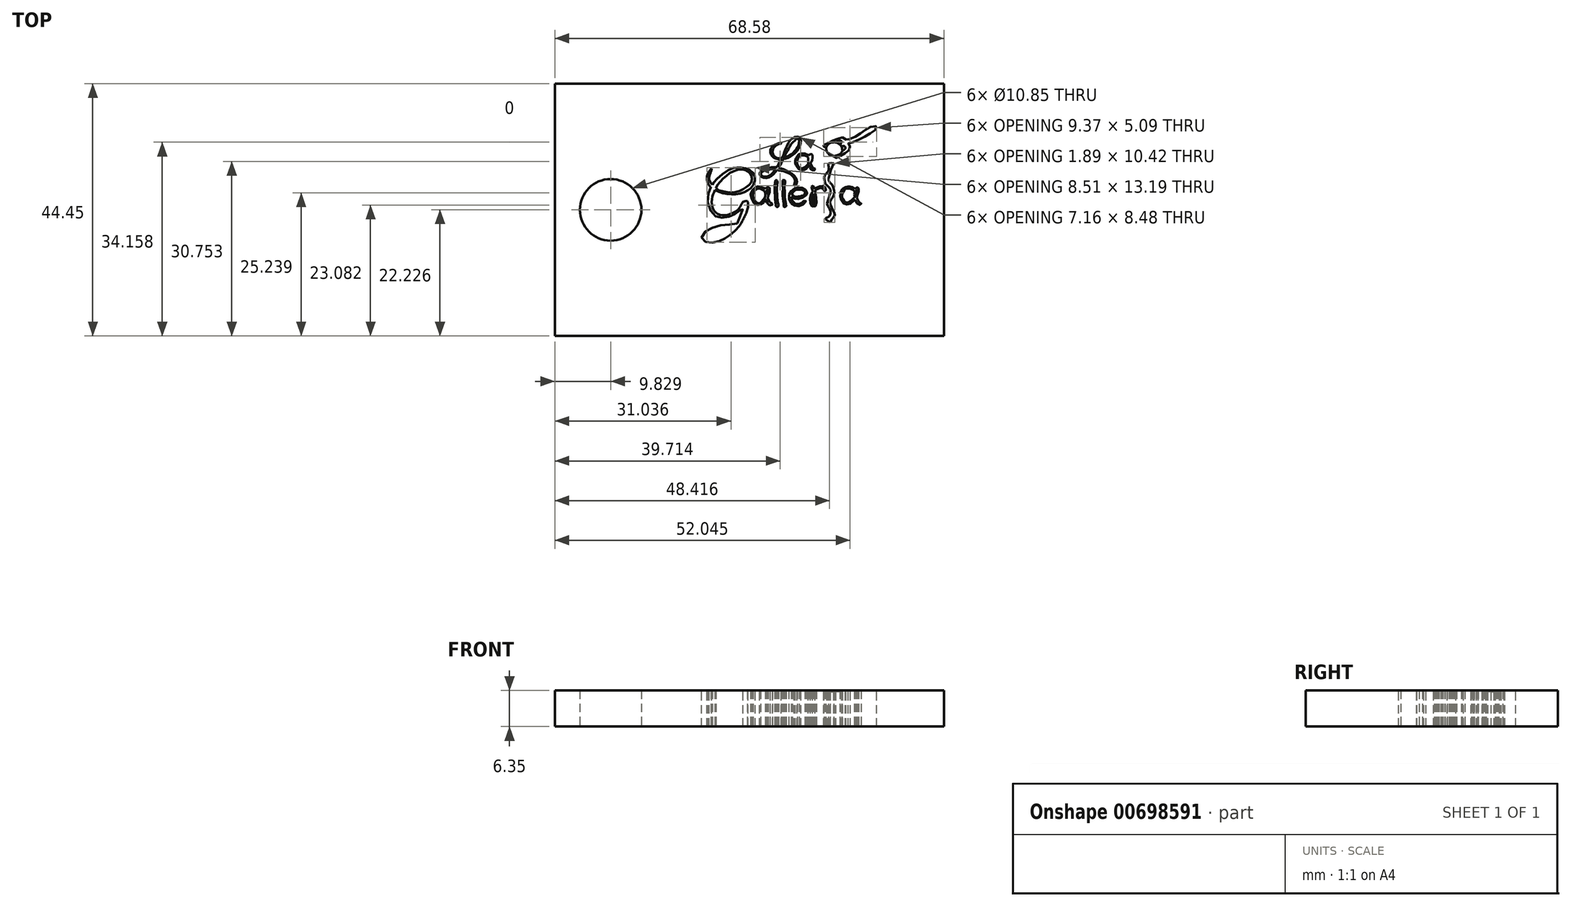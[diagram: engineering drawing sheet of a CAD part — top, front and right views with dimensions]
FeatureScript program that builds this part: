
annotation { "Feature Type Name" : "Feature", "Feature Type Description" : "" }
export const myFeature = defineFeature(function(context is Context, id is Id, definition is map)
    precondition{}
    {
        {
            var Q0;
            Q0=qCreatedBy(makeId("Top.planeOp"),FACE);
            var sketch = newSketch(context, id + "F0", { "sketchPlane" : qUnion([Q0])});
            skLineSegment(sketch, "E0.bottom", {"start": v(-33.84, -40.5) * mm, "end": v(34.74, -40.5) * mm});
            skLineSegment(sketch, "E0.top", {"start": v(-33.84, -84.96) * mm, "end": v(34.74, -84.96) * mm});
            skLineSegment(sketch, "E0.left", {"start": v(-33.84, -40.5) * mm, "end": v(-33.84, -84.96) * mm});
            skLineSegment(sketch, "E0.right", {"start": v(34.74, -40.5) * mm, "end": v(34.74, -84.96) * mm});
            skCircle(sketch, "E1", {"center": v(-24.01, -62.73) * mm, "radius": 5.42 * mm});
            skLineSegment(sketch, "E2", {"start": v(34.74, -62.73) * mm, "end": v(-33.84, -62.73) * mm, "construction": true});
            skSolve(sketch);
        }
        {
            var Q0;
            Q0=makeQuery(id+"F0.imprint","IMPRINT",FACE,{"disambiguationData":[TD([[makeQuery(id+"F0.imprint","IMPRINT",EDGE,{"derivedFrom":sQuery(id+"F0.wireOp",EDGE,"E0.bottom")}),-1.0]])]});
            extrude(context, id + "F1", {"entities" : qUnion([Q0]), "depth" : 6.35 * mm, "offsetDistance" : 25.4 * mm});
        }
        {
            var Q0;
            Q0=qCreatedBy(makeId("Top.planeOp"),FACE);
            var sketch = newSketch(context, id + "F2", { "sketchPlane" : qUnion([Q0])});
            skFitSpline(sketch, "E3", {"points": [v(8.83, -74.2) * mm, v(6.32, -74.67) * mm, v(3.86, -74.8) * mm, v(2.14, -74.58) * mm, v(0.76, -74.1) * mm, v(-0.5, -72.85) * mm, v(-0.7, -72.2) * mm, v(-0.7, -71.6) * mm, v(-0.36, -71.21) * mm, v(0.02, -71) * mm, v(-0.54, -70.7) * mm, v(-1.05, -69.92) * mm, v(-1.31, -68.93) * mm, v(-1.01, -67.85) * mm, v(-0.54, -67.2) * mm, v(-0.1, -66.98) * mm, v(-0.23, -66.55) * mm, v(-0.23, -66.04) * mm, v(0.02, -65.65) * mm, v(0.28, -65.26) * mm, v(0.71, -64.91) * mm, v(1.45, -64.36) * mm, v(2.06, -64.36) * mm, v(2.61, -64.36) * mm, v(3.78, -63.96) * mm, v(4.81, -64.36) * mm, v(4.81, -64.36) * mm, v(5.9, -65.13) * mm, v(6.32, -66.04) * mm, v(6.84, -66.42) * mm, v(7.62, -66.77) * mm, v(8.05, -67.2) * mm], "startDerivative": vector(-44.88, -9.77) * mm, "endDerivative": vector(13.58, -17.29) * mm});
            skFitSpline(sketch, "E4", {"points": [v(7.93, -67.04) * mm, v(7.02, -67.04) * mm, v(6.32, -66.42) * mm, v(5.46, -65.6) * mm, v(4.94, -65.09) * mm, v(3.78, -64.36) * mm, v(2.61, -64.36) * mm, v(1.8, -64.91) * mm, v(0.71, -65.34) * mm, v(0.33, -66.42) * mm, v(0.71, -67.59) * mm, v(1.5, -68.06) * mm, v(2, -68.28) * mm, v(1.62, -68.67) * mm, v(0.71, -68.1) * mm, v(0.24, -67.46) * mm, v(-0.1, -66.98) * mm], "startDerivative": vector(-15.93, -2.47) * mm, "endDerivative": vector(-7.03, 9.38) * mm});
            skFitSpline(sketch, "E5", {"points": [v(15.3, -54.51) * mm, v(14.74, -55.9) * mm, v(14.52, -56.76) * mm, v(14.44, -57.58) * mm, v(15, -58.27) * mm, v(15.39, -59.26) * mm, v(15.43, -59.86) * mm, v(15.09, -60.6) * mm, v(14.65, -61.33) * mm, v(14.87, -62.15) * mm, v(15.26, -62.97) * mm, v(15.52, -63.66) * mm, v(15, -64.36) * mm, v(14.3, -65.26) * mm, v(13.83, -64.36) * mm, v(14.4, -63.96) * mm, v(14.7, -63.53) * mm, v(14.74, -63.06) * mm, v(14.52, -62.45) * mm, v(14.14, -61.72) * mm, v(14.4, -60.86) * mm], "startDerivative": vector(-9.76, -21.95) * mm, "endDerivative": vector(8.6, 17.1) * mm});
            skFitSpline(sketch, "E6", {"points": [v(14.4, -60.86) * mm, v(14.65, -59.86) * mm, v(14.65, -59) * mm, v(13.96, -58.27) * mm, v(13.66, -57.5) * mm, v(13.75, -56.63) * mm, v(14.4, -55.8) * mm, v(14.4, -54.99) * mm, v(14.4, -54.6) * mm, v(15.3, -54.51) * mm], "startDerivative": vector(2.25, 8.11) * mm, "endDerivative": vector(10.26, -0.46) * mm});
            skFitSpline(sketch, "E7", {"points": [v(14.67, -64.93) * mm, v(16.12, -64.36) * mm, v(17.07, -63.96) * mm, v(17.8, -63.92) * mm, v(18.8, -64.36) * mm, v(19.36, -65.26) * mm, v(19.53, -66.47) * mm, v(19.62, -66.81) * mm, v(19.14, -67.5) * mm, v(19.49, -67.46) * mm, v(19.83, -67.68) * mm, v(19.83, -68.06) * mm, v(20.3, -68.02) * mm, v(20.87, -68.02) * mm, v(20.87, -68.58) * mm, v(20.82, -68.8) * mm, v(21.26, -68.62) * mm, v(21.69, -68.8) * mm, v(21.56, -69.32) * mm, v(20.74, -69.88) * mm, v(21.13, -70.3) * mm, v(21.64, -70.83) * mm, v(21.77, -71.6) * mm, v(21.13, -72.5) * mm, v(19.7, -73.46) * mm, v(18.15, -74.28) * mm, v(16.42, -74.58) * mm, v(14.61, -74.7) * mm, v(12.67, -74.54) * mm, v(11.29, -73.89) * mm, v(10.04, -73.93) * mm, v(8.83, -74.2) * mm], "startDerivative": vector(35.2, 13.5) * mm, "endDerivative": vector(-31.28, -7.01) * mm});
            skFitSpline(sketch, "E8", {"points": [v(13.83, -64.36) * mm, v(12.71, -63.96) * mm, v(10.73, -63.49) * mm, v(8, -63.96) * mm, v(6.8, -65.13) * mm, v(6.32, -66.04) * mm], "startDerivative": vector(-6.29, 2.24) * mm, "endDerivative": vector(-2.62, -5.65) * mm});
            skFitSpline(sketch, "E9", {"points": [v(0.24, -67.46) * mm, v(0.24, -68.5) * mm, v(-0.2, -69.23) * mm, v(0.24, -70.3) * mm, v(1.23, -71) * mm, v(3.86, -71.34) * mm, v(6.32, -71) * mm, v(8.1, -69.83) * mm, v(8.87, -68.58) * mm, v(9.09, -68.1) * mm, v(9.6, -68.1) * mm, v(9.43, -69.1) * mm, v(8.7, -70.05) * mm, v(7.06, -71.43) * mm, v(5.6, -72) * mm, v(3.95, -71.95) * mm, v(2.48, -71.82) * mm, v(0.71, -71.47) * mm, v(0.02, -71) * mm], "startDerivative": vector(3.87, -23.1) * mm, "endDerivative": vector(-13.05, 11.9) * mm});
            skFitSpline(sketch, "E10", {"points": [v(6.46, -65.74) * mm, v(6.84, -65.74) * mm, v(7.16, -65.13) * mm, v(8.05, -64.56) * mm, v(8.95, -64.15) * mm, v(9.81, -64) * mm, v(10.76, -63.93) * mm, v(11.8, -64.04) * mm, v(12.81, -64.36) * mm, v(13.48, -64.94) * mm, v(13.4, -65.74) * mm, v(12.9, -66.04) * mm, v(13.03, -65.5) * mm, v(12.81, -65.13) * mm, v(12.23, -64.9) * mm, v(11.02, -65.13) * mm, v(10.57, -65.33) * mm], "startDerivative": vector(9.8, -2.5) * mm, "endDerivative": vector(-7.4, -3.9) * mm});
            skFitSpline(sketch, "E11", {"points": [v(19.53, -66.47) * mm, v(19.07, -66.24) * mm, v(18.47, -66.47) * mm, v(18.36, -66.47) * mm], "startDerivative": vector(-1.06, 0.92) * mm, "endDerivative": vector(-0.47, 0.13) * mm});
            skFitSpline(sketch, "E12", {"points": [v(18.47, -66.47) * mm, v(18.7, -65.79) * mm, v(18.66, -65.29) * mm, v(18.47, -64.99) * mm, v(17.71, -64.77) * mm, v(16.7, -64.82) * mm, v(15.66, -65.25) * mm, v(14.82, -65.57) * mm, v(14.15, -65.87) * mm, v(13.53, -66.22) * mm, v(12.5, -66.8) * mm, v(11.86, -67.08) * mm, v(11.28, -67.32) * mm, v(10.63, -67.21) * mm, v(11.28, -66.8) * mm, v(11.41, -66.47) * mm, v(11.67, -66.47) * mm, v(12.34, -66.47) * mm, v(12.9, -66.04) * mm], "startDerivative": vector(5.46, 12.2) * mm, "endDerivative": vector(9.08, 9.58) * mm});
            skFitSpline(sketch, "E13", {"points": [v(0.21, -71.17) * mm, v(0.52, -71.38) * mm, v(0.21, -71.48) * mm, v(-0.07, -71.83) * mm, v(0, -72.52) * mm, v(0.21, -73.06) * mm, v(0.84, -73.4) * mm, v(1.74, -73.77) * mm, v(2.76, -73.99) * mm, v(3.86, -73.96) * mm, v(4.92, -74.03) * mm, v(5.7, -74) * mm, v(6.32, -74.03) * mm, v(7.25, -74.03) * mm, v(7.46, -73.88) * mm, v(6.51, -73.7) * mm, v(5.97, -73.6) * mm, v(5.2, -73.34) * mm, v(5, -73.17) * mm, v(4.85, -73.3) * mm, v(4.23, -73.34) * mm, v(3.64, -73.27) * mm, v(3.17, -73.25) * mm, v(2.35, -73.1) * mm, v(1.68, -72.84) * mm, v(1.16, -72.52) * mm, v(0.92, -72.02) * mm, v(0.91, -71.54) * mm, v(0.71, -71.47) * mm], "startDerivative": vector(17.38, -8.75) * mm, "endDerivative": vector(-11.59, 0.94) * mm});
            skFitSpline(sketch, "E14", {"points": [v(2.05, -71.77) * mm, v(1.87, -71.95) * mm, v(1.85, -72.24) * mm, v(2.09, -72.41) * mm, v(2.74, -72.52) * mm, v(3.34, -72.6) * mm, v(3.77, -72.67) * mm, v(3.95, -72.7) * mm, v(3.66, -72.45) * mm, v(3.38, -72.15) * mm, v(3.22, -71.89) * mm], "startDerivative": vector(-2.45, -1.9) * mm, "endDerivative": vector(-1.73, 2.9) * mm});
            skFitSpline(sketch, "E15", {"points": [v(3.95, -72.7) * mm, v(4.36, -72.89) * mm, v(4.77, -73.12) * mm, v(5, -73.17) * mm], "startDerivative": vector(1.1, -0.47) * mm, "endDerivative": vector(0.85, -0.05) * mm});
            skFitSpline(sketch, "E16", {"points": [v(7.46, -73.88) * mm, v(8.2, -73.88) * mm, v(9.3, -73.7) * mm, v(10.44, -73.42) * mm, v(11.02, -73.17) * mm, v(11.67, -72.7) * mm, v(12.08, -72.22) * mm, v(12.14, -71.63) * mm, v(12.3, -71.16) * mm, v(12.3, -71.03) * mm, v(11.78, -70.92) * mm, v(10.83, -70.77) * mm, v(10.33, -70.68) * mm, v(9.43, -70.43) * mm, v(8.84, -70.23) * mm, v(8.5, -70.24) * mm, v(7.7, -70.95) * mm], "startDerivative": vector(10.73, -0.44) * mm, "endDerivative": vector(-11.05, -11.71) * mm});
            skFitSpline(sketch, "E17", {"points": [v(4.61, -72) * mm, v(5, -72.32) * mm, v(5.54, -72.7) * mm, v(6.32, -73) * mm, v(6.51, -73.17) * mm, v(7.46, -73.42) * mm, v(8.48, -73.4) * mm, v(9.53, -73.17) * mm, v(10.44, -72.97) * mm, v(11.2, -72.24) * mm, v(11.67, -71.74) * mm, v(11.78, -70.92) * mm, v(11.43, -70.87) * mm, v(11.03, -70.8) * mm, v(10.94, -71.35) * mm, v(10.6, -71.98) * mm, v(9.88, -72.37) * mm, v(8.65, -72.7) * mm, v(8, -72.7) * mm, v(6.82, -72.48) * mm, v(6.32, -72.26) * mm, v(5.9, -71.94) * mm, v(6.32, -71.81) * mm, v(6.84, -71.56) * mm, v(7.23, -71.98) * mm, v(8, -72.13) * mm, v(9.04, -71.94) * mm, v(9.73, -71.57) * mm, v(10.16, -71.2) * mm, v(10.33, -70.68) * mm, v(9.98, -70.6) * mm, v(9.59, -70.48) * mm, v(9.43, -70.92) * mm, v(8.95, -71.3) * mm, v(8, -71.57) * mm, v(7.27, -71.28) * mm, v(7.7, -70.95) * mm, v(8, -70.95) * mm, v(8.4, -70.95) * mm, v(8.89, -70.68) * mm, v(9.12, -70.32) * mm], "startDerivative": vector(17.49, -14.44) * mm, "endDerivative": vector(9.15, 18.57) * mm});
            skFitSpline(sketch, "E18", {"points": [v(9, -69.73) * mm, v(9.3, -69.98) * mm, v(9.98, -70.13) * mm, v(10.48, -70.13) * mm, v(11.67, -70.43) * mm, v(12.3, -70.6) * mm, v(13.56, -70.68) * mm, v(14.52, -70.68) * mm, v(15.46, -70.32) * mm, v(16.96, -69.94) * mm, v(17.9, -69.46) * mm, v(19, -68.96) * mm, v(20.3, -68.02) * mm], "startDerivative": vector(4.52, -5.15) * mm, "endDerivative": vector(12.09, 9.8) * mm});
            skFitSpline(sketch, "E19", {"points": [v(20.82, -68.8) * mm, v(20.5, -68.96) * mm, v(19.87, -69.33) * mm, v(19.1, -69.67) * mm, v(18.64, -69.89) * mm, v(17.83, -70.25) * mm, v(17.22, -70.48) * mm, v(16.32, -70.67) * mm, v(15.46, -70.95) * mm, v(14.02, -71.16) * mm, v(12.78, -71.05) * mm, v(12.3, -71.03) * mm, v(12.2, -71.4) * mm, v(12.13, -71.77) * mm, v(12.5, -71.78) * mm, v(13, -71.63) * mm, v(13.36, -71.43) * mm, v(13.4, -71.16) * mm], "startDerivative": vector(-6.76, -3.18) * mm, "endDerivative": vector(-0.09, 7.44) * mm});
            skFitSpline(sketch, "E20", {"points": [v(9.37, -69.21) * mm, v(9.88, -69.39) * mm, v(10.44, -69.53) * mm, v(10.97, -69.73) * mm, v(11.93, -70.08) * mm, v(12.77, -70.25) * mm, v(13.27, -70.33) * mm, v(14.47, -70.14) * mm, v(15.09, -69.82) * mm, v(15.94, -69.46) * mm, v(16.88, -68.96) * mm, v(18.01, -68.56) * mm, v(18.7, -68.23) * mm, v(19.3, -67.5) * mm, v(19.2, -67.4) * mm, v(17.94, -67.73) * mm, v(17.24, -68.08) * mm, v(16.56, -68.36) * mm, v(16.46, -68.42) * mm, v(16.28, -68.67) * mm, v(16.04, -68.96) * mm, v(15.55, -69.14) * mm, v(15.13, -69.22) * mm, v(14.73, -69.49) * mm, v(14.13, -69.73) * mm, v(13.7, -69.82) * mm, v(13.24, -69.82) * mm, v(12.83, -69.6) * mm, v(12.14, -69.35) * mm, v(11.19, -68.96) * mm, v(10.26, -68.8) * mm, v(9.9, -68.8) * mm, v(9.56, -68.8) * mm], "startDerivative": vector(17.22, -6.4) * mm, "endDerivative": vector(-15.28, 0.15) * mm});
            skFitSpline(sketch, "E21", {"points": [v(0.37, -66.83) * mm, v(0.79, -66.8) * mm, v(1.2, -66.77) * mm, v(1.68, -66.66) * mm, v(2.42, -66.46) * mm, v(3.32, -66.21) * mm, v(4.18, -66.17) * mm, v(5, -66.1) * mm, v(5.6, -66) * mm, v(5.92, -66.03) * mm], "startDerivative": vector(4.5, 0.34) * mm, "endDerivative": vector(3.66, -0.47) * mm});
            skFitSpline(sketch, "E22", {"points": [v(1.2, -66.77) * mm, v(1.2, -66.42) * mm, v(1.38, -65.88) * mm, v(1.74, -65.5) * mm, v(2.32, -65.4) * mm, v(3, -65.57) * mm, v(3.85, -65.82) * mm, v(4.5, -65.9) * mm, v(5.13, -66.08) * mm], "startDerivative": vector(-0.3, 3.46) * mm, "endDerivative": vector(4.87, -1.51) * mm});
            skFitSpline(sketch, "E23", {"points": [v(0.51, -67.25) * mm, v(1.2, -67.2) * mm, v(1.94, -67.1) * mm, v(3.35, -66.77) * mm, v(4.52, -66.42) * mm, v(6.32, -66.42) * mm], "startDerivative": vector(4.45, 0.36) * mm, "endDerivative": vector(7.71, -0.5) * mm});
            skFitSpline(sketch, "E24", {"points": [v(0.71, -67.59) * mm, v(1.73, -67.59) * mm, v(2.93, -67.43) * mm, v(4.18, -67.2) * mm, v(4.85, -67.04) * mm, v(6.47, -66.82) * mm, v(6.7, -66.82) * mm], "startDerivative": vector(5.79, -0.2) * mm, "endDerivative": vector(1.9, -0.15) * mm});
            skFitSpline(sketch, "E25", {"points": [v(2, -68.28) * mm, v(2.6, -68.06) * mm, v(3.6, -67.9) * mm, v(3.84, -67.74) * mm, v(4.26, -67.59) * mm, v(4.76, -67.45) * mm, v(5, -67.45) * mm, v(5.23, -67.37) * mm, v(5.63, -67.24) * mm, v(6.5, -67.1) * mm, v(7.6, -67.1) * mm], "startDerivative": vector(4.6, 2.3) * mm, "endDerivative": vector(7.8, -0.3) * mm});
            skFitSpline(sketch, "E26", {"points": [v(3.6, -67.9) * mm, v(3.39, -68.26) * mm, v(3.3, -68.51) * mm, v(3.45, -69.06) * mm, v(3.92, -69.4) * mm, v(4.5, -69.57) * mm, v(5.05, -69.62) * mm, v(5.79, -69.42) * mm, v(6.32, -68.94) * mm, v(6.45, -68.4) * mm, v(6.12, -67.9) * mm, v(5.56, -67.59) * mm, v(4.87, -67.45) * mm], "startDerivative": vector(-3.32, -5.44) * mm, "endDerivative": vector(-7.66, 1.04) * mm});
            skFitSpline(sketch, "E27", {"points": [v(0.71, -68.1) * mm, v(0.71, -68.57) * mm, v(0.58, -69.13) * mm, v(0.6, -69.64) * mm, v(0.84, -70.07) * mm, v(1.4, -70.43) * mm, v(2.22, -70.67) * mm, v(2.88, -70.7) * mm, v(3.6, -70.75) * mm, v(4.13, -70.72) * mm, v(5, -70.6) * mm, v(5.79, -70.4) * mm, v(6.72, -70) * mm, v(7.54, -69.48) * mm, v(8.25, -68.79) * mm, v(8.48, -68.1) * mm, v(8.5, -67.73) * mm], "startDerivative": vector(0.7, -8.8) * mm, "endDerivative": vector(0.25, 7.53) * mm});
            skFitSpline(sketch, "E28", {"points": [v(1.5, -68.67) * mm, v(1.8, -68.79) * mm, v(2.46, -68.67) * mm, v(3.3, -68.51) * mm], "startDerivative": vector(1.1, -0.65) * mm, "endDerivative": vector(2.11, 0.34) * mm});
            skFitSpline(sketch, "E29", {"points": [v(6.12, -67.9) * mm, v(6.48, -67.77) * mm, v(7.2, -67.73) * mm, v(8, -67.73) * mm, v(8.5, -67.73) * mm, v(9.16, -67.9) * mm, v(10.07, -68.28) * mm, v(10.94, -68.67) * mm, v(12.39, -69.1) * mm, v(13.4, -69.25) * mm, v(14.73, -69.26) * mm, v(15.13, -69.22) * mm], "startDerivative": vector(5.23, 2.4) * mm, "endDerivative": vector(5.1, 0.8) * mm});
            skFitSpline(sketch, "E30", {"points": [v(8.05, -67.2) * mm, v(8.84, -67.37) * mm, v(10.03, -67.73) * mm, v(10.84, -68.1) * mm, v(11.9, -68.51) * mm, v(13.53, -68.93) * mm, v(14, -69.05) * mm], "startDerivative": vector(4.93, -0.95) * mm, "endDerivative": vector(3.36, -0.83) * mm});
            skFitSpline(sketch, "E31", {"points": [v(6.6, -65.78) * mm, v(7.34, -65.9) * mm, v(7.95, -66.08) * mm, v(8.44, -66.21) * mm], "startDerivative": vector(2.05, -0.29) * mm, "endDerivative": vector(1.57, -0.4) * mm});
            skFitSpline(sketch, "E32", {"points": [v(6.6, -66.3) * mm, v(7.04, -66.24) * mm, v(7.59, -66.37) * mm, v(8.3, -66.58) * mm, v(8.69, -66.8) * mm], "startDerivative": vector(1.9, 0.45) * mm, "endDerivative": vector(1.55, -0.98) * mm});
            skFitSpline(sketch, "E33", {"points": [v(7.34, -65.9) * mm, v(7.59, -65.48) * mm, v(8.3, -65.03) * mm, v(9.72, -64.6) * mm, v(11.07, -64.36) * mm, v(12.7, -64.58) * mm, v(13.15, -64.94) * mm, v(13.4, -65.74) * mm], "startDerivative": vector(2, 4.32) * mm, "endDerivative": vector(1.5, -6.77) * mm});
            skFitSpline(sketch, "E34", {"points": [v(11.32, -65.74) * mm, v(11.57, -65.74) * mm, v(11.94, -65.74) * mm, v(12.3, -66.04) * mm, v(12.34, -66.47) * mm], "startDerivative": vector(1.18, -0.06) * mm, "endDerivative": vector(-0.17, -1.68) * mm});
            skFitSpline(sketch, "E35", {"points": [v(8.44, -66.21) * mm, v(8.44, -66.02) * mm, v(8.67, -65.65) * mm, v(9.05, -65.39) * mm, v(9.64, -65.21) * mm, v(10.25, -65.22) * mm, v(10.7, -65.35) * mm, v(11.15, -65.59) * mm, v(11.38, -65.97) * mm, v(11.41, -66.47) * mm, v(11.14, -66.91) * mm, v(10.46, -67.21) * mm, v(9.72, -67.26) * mm, v(9.1, -67.1) * mm, v(8.69, -66.8) * mm, v(8.44, -66.52) * mm, v(8.36, -66.17) * mm, v(8.69, -65.6) * mm], "startDerivative": vector(-0.8, 4.83) * mm, "endDerivative": vector(6.62, 8.74) * mm});
            skFitSpline(sketch, "E36", {"points": [v(7.62, -66.77) * mm, v(7.91, -66.77) * mm, v(8.44, -66.77) * mm, v(8.97, -67.03) * mm], "startDerivative": vector(1.02, -0.04) * mm, "endDerivative": vector(1.37, -0.87) * mm});
            skFitSpline(sketch, "E37", {"points": [v(9.86, -67.26) * mm, v(10.5, -67.54) * mm, v(11.2, -67.73) * mm, v(11.94, -67.77) * mm, v(12.9, -67.49) * mm, v(14.07, -66.86) * mm, v(15.4, -66.21) * mm, v(16.72, -65.62) * mm, v(17.48, -65.48) * mm, v(17.86, -65.48) * mm, v(18.16, -65.74) * mm, v(18.14, -66.28) * mm, v(17.8, -66.64) * mm, v(17.45, -67.04) * mm, v(17.25, -67.27) * mm, v(17.2, -67.47) * mm, v(16.85, -67.7) * mm, v(16.47, -67.9) * mm], "startDerivative": vector(10.19, -4.86) * mm, "endDerivative": vector(-7.63, -3.92) * mm});
            skFitSpline(sketch, "E38", {"points": [v(1.16, -68.52) * mm, v(1.17, -69) * mm, v(1.5, -69.63) * mm, v(2.33, -70.06) * mm, v(3.44, -70.17) * mm, v(4.62, -70.08) * mm, v(6.06, -69.6) * mm, v(7.22, -68.95) * mm, v(7.89, -68.32) * mm, v(8, -67.73) * mm, v(7.4, -67.73) * mm, v(7.2, -68.18) * mm, v(6.67, -68.67) * mm, v(6.4, -68.78) * mm], "startDerivative": vector(-0.61, -7.8) * mm, "endDerivative": vector(-4.96, -1.65) * mm});
            skFitSpline(sketch, "E39", {"points": [v(1.8, -68.79) * mm, v(1.8, -69.08) * mm, v(2.3, -69.47) * mm, v(3.1, -69.63) * mm, v(4.09, -69.55) * mm, v(4.25, -69.5) * mm], "startDerivative": vector(-0.47, -2) * mm, "endDerivative": vector(1.1, 0.45) * mm});
            skFitSpline(sketch, "E40", {"points": [v(3.02, -68.56) * mm, v(3.02, -68.79) * mm, v(3.02, -69.04) * mm, v(3.5, -69.13) * mm], "startDerivative": vector(0.06, -0.76) * mm, "endDerivative": vector(1.51, -0.02) * mm});
            skFitSpline(sketch, "E41", {"points": [v(10.84, -68.1) * mm, v(11.54, -68.28) * mm, v(12, -68.3) * mm, v(12.44, -68.3) * mm, v(12.98, -68.26) * mm, v(13.36, -68.24) * mm], "startDerivative": vector(3.06, -0.86) * mm, "endDerivative": vector(2.07, 0.14) * mm});
            skFitSpline(sketch, "E42", {"points": [v(13.87, -69.01) * mm, v(13.53, -68.69) * mm, v(13.36, -68.24) * mm, v(13.36, -67.78) * mm, v(13.87, -67.3) * mm, v(14.74, -67.12) * mm, v(15.65, -67.21) * mm, v(16.1, -67.43) * mm, v(16.6, -67.84) * mm, v(16.56, -68.36) * mm], "startDerivative": vector(-3.96, 3) * mm, "endDerivative": vector(-1.48, -5.34) * mm});
            skFitSpline(sketch, "E43", {"points": [v(15.3, -67.14) * mm, v(15.94, -66.86) * mm, v(16.47, -66.7) * mm, v(16.88, -66.9) * mm, v(16.85, -67.7) * mm], "startDerivative": vector(2.48, 1.12) * mm, "endDerivative": vector(-0.7, -3.3) * mm});
            skFitSpline(sketch, "E44", {"points": [v(17.2, -67.47) * mm, v(17.78, -67.04) * mm, v(18.39, -66.47) * mm], "startDerivative": vector(1.22, 0.84) * mm, "endDerivative": vector(1.16, 1.15) * mm});
            skFitSpline(sketch, "E45", {"points": [v(12.08, -72.22) * mm, v(12.89, -72.22) * mm, v(13.87, -72.22) * mm, v(14.26, -72.04) * mm, v(14.57, -71.6) * mm, v(14.6, -71.11) * mm], "startDerivative": vector(3.36, 0.06) * mm, "endDerivative": vector(-0.11, 2.82) * mm});
            skFitSpline(sketch, "E46", {"points": [v(11.81, -72.57) * mm, v(12.5, -72.9) * mm, v(13.87, -73) * mm, v(15.14, -72.57) * mm, v(15.65, -71.97) * mm, v(15.94, -71.1) * mm, v(16.13, -70.73) * mm], "startDerivative": vector(3.96, -2.38) * mm, "endDerivative": vector(1.76, 2.72) * mm});
            skFitSpline(sketch, "E47", {"points": [v(11.22, -73.04) * mm, v(12.08, -73.5) * mm, v(15.18, -73.17) * mm, v(16.47, -72.72) * mm, v(17.2, -71.82) * mm, v(17.22, -70.48) * mm], "startDerivative": vector(4.05, -3.61) * mm, "endDerivative": vector(-0.93, 7.48) * mm});
            skFitSpline(sketch, "E48", {"points": [v(11.29, -73.89) * mm, v(12.5, -73.53) * mm], "startDerivative": vector(1.2, 0.36) * mm, "endDerivative": vector(1.2, 0.36) * mm});
            skFitSpline(sketch, "E49", {"points": [v(14.32, -73.32) * mm, v(16.47, -73.17) * mm, v(17.76, -72.52) * mm, v(18.39, -71.27) * mm, v(18.64, -69.89) * mm], "startDerivative": vector(7.77, 0.08) * mm, "endDerivative": vector(0.83, 5.86) * mm});
            skFitSpline(sketch, "E50", {"points": [v(18.58, -70.35) * mm, v(19.3, -70.1) * mm, v(20.1, -69.89) * mm, v(20.74, -69.88) * mm], "startDerivative": vector(2.07, 0.73) * mm, "endDerivative": vector(2, -0.1) * mm});
            skFitSpline(sketch, "E51", {"points": [v(18.52, -70.68) * mm, v(20.1, -70.35) * mm, v(20.74, -70.8) * mm, v(20.74, -71.53) * mm, v(20.1, -72.22) * mm, v(19, -73.17) * mm, v(17.45, -73.89) * mm, v(15.94, -74.07) * mm, v(14.12, -74.11) * mm, v(12.25, -73.89) * mm, v(11.69, -73.77) * mm], "startDerivative": vector(15.22, 5.29) * mm, "endDerivative": vector(-6.94, 1.67) * mm});
            skFitSpline(sketch, "E52", {"points": [v(13.87, -73.4) * mm, v(15.2, -73.5) * mm, v(16.88, -73.5) * mm, v(18.82, -72.48) * mm, v(19.83, -71.55) * mm, v(19.83, -71.1) * mm, v(18.64, -71.07) * mm, v(18.39, -71.27) * mm], "startDerivative": vector(8.34, -0.4) * mm, "endDerivative": vector(-2, -2.83) * mm});
            skFitSpline(sketch, "E53", {"points": [v(13.96, -51.96) * mm, v(14.05, -51.6) * mm, v(14.34, -51.19) * mm, v(14.8, -50.9) * mm, v(15.65, -50.84) * mm, v(16.29, -51.06) * mm, v(16.7, -51.45) * mm, v(16.85, -51.93) * mm, v(16.72, -52.56) * mm, v(16.37, -52.92) * mm, v(15.65, -53.2) * mm, v(14.96, -53.22) * mm, v(14.47, -52.96) * mm, v(14.04, -52.5) * mm, v(13.96, -51.96) * mm]});
            skFitSpline(sketch, "E54", {"points": [v(13.63, -51.3) * mm, v(14.35, -50.96) * mm, v(14.85, -50.7) * mm, v(15.5, -50.38) * mm, v(16.37, -50.1) * mm, v(16.97, -49.98) * mm, v(17.45, -50.3) * mm, v(17.45, -50.42) * mm, v(18.01, -50.32) * mm, v(19.12, -49.83) * mm, v(20, -49.27) * mm, v(20.98, -48.57) * mm, v(21.85, -48.1) * mm, v(22.69, -47.97) * mm, v(22.89, -48.29) * mm, v(22.26, -48.92) * mm, v(21.23, -49.6) * mm, v(20.1, -50.17) * mm, v(19.08, -50.65) * mm, v(18.16, -51) * mm, v(17.85, -51.1) * mm, v(18.16, -51.57) * mm, v(18.16, -51.96) * mm, v(17.84, -52.37) * mm, v(17.22, -52.84) * mm, v(16.6, -53.19) * mm, v(15.94, -53.49) * mm, v(15.43, -53.6) * mm, v(15.29, -53.34) * mm], "startDerivative": vector(20.07, 9.1) * mm, "endDerivative": vector(-4.03, 14.45) * mm});
            skFitSpline(sketch, "E55", {"points": [v(16.82, -52.3) * mm, v(17.22, -52.1) * mm, v(17.35, -51.81) * mm, v(17.22, -51.51) * mm, v(16.77, -51.56) * mm], "startDerivative": vector(1.69, 0.6) * mm, "endDerivative": vector(-1.91, -0.59) * mm});
            skFitSpline(sketch, "E56", {"points": [v(16.37, -51.12) * mm, v(16.6, -51) * mm, v(16.7, -50.71) * mm, v(16.47, -50.55) * mm, v(16.05, -50.64) * mm, v(15.65, -50.84) * mm], "startDerivative": vector(1.34, 0.52) * mm, "endDerivative": vector(-1.7, -0.91) * mm});
            skFitSpline(sketch, "E57", {"points": [v(13.63, -51.3) * mm, v(13.53, -51.5) * mm, v(13.87, -51.7) * mm, v(14.05, -51.6) * mm], "startDerivative": vector(-0.64, -0.67) * mm, "endDerivative": vector(0.48, 0.5) * mm});
            skFitSpline(sketch, "E58", {"points": [v(0.06, -61.14) * mm, v(0.19, -61.42) * mm, v(0.19, -62.24) * mm, v(-0.23, -63.56) * mm, v(-0.8, -64.69) * mm, v(-1.28, -65.54) * mm, v(-2.03, -66.41) * mm, v(-2.7, -66.95) * mm, v(-3.34, -67.47) * mm, v(-4.03, -67.88) * mm, v(-4.78, -68.21) * mm, v(-5.7, -68.47) * mm, v(-6.71, -68.52) * mm, v(-7.64, -68.16) * mm, v(-7.97, -67.52) * mm, v(-7.33, -66.62) * mm, v(-6.3, -66) * mm, v(-4.83, -65.51) * mm, v(-3.19, -65.33) * mm, v(-1.82, -65.23) * mm, v(-1.23, -64.04) * mm, v(-0.87, -63.04) * mm, v(-0.69, -62.4) * mm, v(-1.33, -62.94) * mm, v(-2.03, -63.43) * mm, v(-2.83, -63.81) * mm, v(-3.67, -64.04) * mm, v(-4.73, -64.1) * mm, v(-5.63, -63.79) * mm, v(-6.45, -62.8) * mm, v(-6.92, -61.27) * mm, v(-6.71, -59.7) * mm, v(-6.33, -58.7) * mm], "startDerivative": vector(8.57, -14.22) * mm, "endDerivative": vector(12.84, 29.36) * mm});
            skFitSpline(sketch, "E59", {"points": [v(-6.07, -58.36) * mm, v(-5.68, -57.69) * mm, v(-2.98, -55.6) * mm, v(-1.54, -55.27) * mm, v(-0.12, -55.42) * mm, v(1.03, -56.14) * mm, v(1.45, -57.38) * mm, v(0.83, -58.74) * mm, v(-0.07, -59.46) * mm, v(-1.36, -59.9) * mm, v(-2.9, -60) * mm, v(-4.3, -59.8) * mm, v(-5.63, -59.2) * mm], "startDerivative": vector(3.46, 9.46) * mm, "endDerivative": vector(-15.92, 8.16) * mm});
            skFitSpline(sketch, "E60", {"points": [v(-5.63, -59.2) * mm, v(-5.96, -60.1) * mm, v(-6.2, -61.27) * mm, v(-5.91, -62.7) * mm, v(-5.12, -63.48) * mm, v(-3.98, -63.71) * mm, v(-2.72, -63.4) * mm, v(-1.44, -62.6) * mm, v(-0.66, -61.37) * mm, v(0.06, -61.14) * mm], "startDerivative": vector(-3.48, -8.83) * mm, "endDerivative": vector(8.82, 0.75) * mm});
            skFitSpline(sketch, "E61", {"points": [v(-1.05, -65.16) * mm, v(0.28, -65.26) * mm], "startDerivative": vector(1.34, -0.1) * mm, "endDerivative": vector(1.34, -0.1) * mm});
            skFitSpline(sketch, "E62", {"points": [v(-1.28, -65.54) * mm, v(0.02, -65.65) * mm], "startDerivative": vector(1.3, -0.1) * mm, "endDerivative": vector(1.3, -0.1) * mm});
            skFitSpline(sketch, "E63", {"points": [v(-5.42, -58.89) * mm, v(-4.89, -57.98) * mm, v(-4, -57.07) * mm, v(-2.98, -56.23) * mm, v(-1.74, -55.72) * mm, v(-0.48, -55.67) * mm, v(0.56, -56.21) * mm, v(0.9, -57.07) * mm, v(0.68, -58) * mm, v(0.1, -58.59) * mm, v(-0.8, -59.2) * mm, v(-2.07, -59.61) * mm, v(-3.23, -59.63) * mm, v(-4.4, -59.43) * mm, v(-5.42, -58.89) * mm]});
            skFitSpline(sketch, "E64", {"points": [v(-6.24, -55.46) * mm, v(-6.73, -56.07) * mm, v(-7.05, -57) * mm, v(-6.94, -57.82) * mm, v(-6.59, -58.52) * mm, v(-6.33, -58.7) * mm], "startDerivative": vector(-2.47, -2.62) * mm, "endDerivative": vector(2, -0.92) * mm});
            skFitSpline(sketch, "E65", {"points": [v(-6.24, -55.46) * mm, v(-6.24, -55.65) * mm, v(-6.46, -56.37) * mm, v(-6.66, -57.33) * mm, v(-6.07, -58.36) * mm], "startDerivative": vector(0.14, -1.24) * mm, "endDerivative": vector(2.49, -3.17) * mm});
            skFitSpline(sketch, "E66", {"points": [v(3.34, -59) * mm, v(3.62, -58.7) * mm, v(3.87, -58.7) * mm, v(4.08, -59.2) * mm, v(3.85, -60.1) * mm, v(3.64, -60.52) * mm, v(3.85, -61.1) * mm, v(4.1, -61.47) * mm, v(4.4, -61.57) * mm, v(4.48, -61.82) * mm, v(4.15, -61.96) * mm, v(3.69, -61.66) * mm, v(3.36, -60.99) * mm, v(3.34, -60.75) * mm, v(3.2, -61.15) * mm, v(2.78, -61.61) * mm, v(2.15, -61.87) * mm, v(1.38, -61.7) * mm, v(0.8, -60.75) * mm, v(0.73, -59.66) * mm, v(1.26, -59) * mm, v(1.7, -58.7) * mm, v(2.47, -58.7) * mm, v(3.34, -59) * mm]});
            skFitSpline(sketch, "E67", {"points": [v(3.15, -59.43) * mm, v(2.78, -59.2) * mm, v(2.15, -59) * mm, v(1.61, -59.2) * mm, v(1.17, -59.73) * mm, v(1.12, -60.52) * mm, v(1.57, -61.29) * mm, v(2.06, -61.57) * mm, v(2.54, -61.38) * mm, v(3.08, -60.7) * mm, v(3.2, -60.52) * mm, v(3.15, -59.43) * mm]});
            skFitSpline(sketch, "E68", {"points": [v(3.5, -59.98) * mm, v(3.51, -59.4) * mm, v(3.63, -59.16) * mm, v(3.7, -59.17) * mm, v(3.75, -59.6) * mm, v(3.5, -59.98) * mm]});
            skFitSpline(sketch, "E69", {"points": [v(5.38, -57.6) * mm, v(5.24, -57.5) * mm, v(5.05, -57.53) * mm, v(4.9, -59.15) * mm, v(5, -60.87) * mm, v(5.2, -62.22) * mm, v(5.42, -62.25) * mm, v(5.58, -62.08) * mm, v(5.51, -61.57) * mm, v(5.34, -60.1) * mm, v(5.33, -58.62) * mm, v(5.38, -57.6) * mm]});
            skFitSpline(sketch, "E70", {"points": [v(6.32, -57.54) * mm, v(6.58, -57.49) * mm, v(6.75, -57.63) * mm, v(6.66, -58.31) * mm, v(6.66, -59.51) * mm, v(6.71, -60.8) * mm, v(6.92, -62.1) * mm, v(6.77, -62.2) * mm, v(6.5, -62.18) * mm, v(6.5, -61.94) * mm, v(6.44, -61.3) * mm, v(6.32, -60.09) * mm, v(6.32, -58.34) * mm, v(6.32, -57.54) * mm]});
            skFitSpline(sketch, "E71", {"points": [v(7.82, -60.39) * mm, v(8.37, -60.73) * mm, v(9.05, -60.8) * mm, v(9.97, -60.5) * mm, v(10.47, -60.15) * mm, v(10.6, -59.83) * mm, v(10.39, -59.25) * mm, v(9.92, -58.91) * mm, v(9.14, -58.8) * mm, v(8.56, -58.89) * mm, v(7.89, -59.34) * mm, v(7.43, -60.1) * mm, v(7.51, -61.07) * mm, v(8.11, -61.8) * mm, v(8.82, -62.06) * mm, v(9.64, -61.94) * mm, v(10.41, -61.24) * mm, v(10.24, -61.03) * mm, v(9.97, -61.24) * mm, v(9.65, -61.53) * mm, v(9.25, -61.7) * mm, v(8.63, -61.66) * mm, v(8.06, -61.23) * mm, v(7.82, -60.39) * mm]});
            skFitSpline(sketch, "E72", {"points": [v(8, -60.01) * mm, v(8.4, -60.39) * mm, v(9.17, -60.39) * mm, v(10.06, -60.09) * mm, v(10.26, -59.7) * mm, v(10.06, -59.38) * mm, v(9.51, -59.19) * mm, v(8.73, -59.2) * mm, v(8.23, -59.51) * mm, v(8, -60.01) * mm]});
            skFitSpline(sketch, "E73", {"points": [v(11.37, -58.67) * mm, v(11.5, -58.54) * mm, v(11.61, -58.5) * mm, v(11.84, -58.88) * mm, v(11.9, -59) * mm, v(12.26, -58.82) * mm, v(12.84, -58.62) * mm, v(13.31, -58.53) * mm, v(13.82, -58.8) * mm, v(13.92, -59.08) * mm, v(13.9, -59.35) * mm, v(13.74, -59.43) * mm, v(13.54, -59.28) * mm, v(13.44, -59.01) * mm, v(13.2, -58.89) * mm, v(12.84, -58.92) * mm, v(12.52, -59.05) * mm, v(12.04, -59.3) * mm, v(12.08, -59.77) * mm, v(12.23, -60.88) * mm, v(12.2, -61.9) * mm, v(11.74, -62.23) * mm, v(11.34, -61.92) * mm, v(11.16, -61.04) * mm, v(11.31, -59.94) * mm, v(11.64, -59.54) * mm, v(11.61, -59.27) * mm, v(11.44, -58.98) * mm, v(11.37, -58.67) * mm]});
            skFitSpline(sketch, "E74", {"points": [v(11.72, -59.98) * mm, v(11.85, -60.77) * mm, v(11.86, -61.63) * mm, v(11.76, -61.82) * mm, v(11.61, -61.66) * mm, v(11.49, -61.16) * mm, v(11.54, -60.3) * mm, v(11.72, -59.98) * mm]});
            skFitSpline(sketch, "E75", {"points": [v(18.98, -59.06) * mm, v(18.53, -58.78) * mm, v(18.02, -58.62) * mm, v(17.5, -58.67) * mm, v(16.9, -59.03) * mm, v(16.5, -59.64) * mm, v(16.45, -60.52) * mm, v(16.75, -61.25) * mm, v(17.26, -61.72) * mm, v(17.96, -61.75) * mm, v(18.65, -61.34) * mm, v(19.04, -60.92) * mm, v(19.23, -61.38) * mm, v(19.67, -61.8) * mm, v(20.08, -61.84) * mm, v(20.15, -61.66) * mm, v(20.02, -61.47) * mm, v(19.8, -61.46) * mm, v(19.56, -61.04) * mm, v(19.36, -60.52) * mm, v(19.5, -60.15) * mm, v(19.7, -59.6) * mm, v(19.7, -59.05) * mm, v(19.63, -58.83) * mm, v(19.33, -58.8) * mm, v(18.98, -59.06) * mm]});
            skFitSpline(sketch, "E76", {"points": [v(18.98, -59.47) * mm, v(18.47, -59.12) * mm, v(17.92, -58.98) * mm, v(17.38, -59.06) * mm, v(16.96, -59.6) * mm, v(16.74, -60.25) * mm, v(17.06, -61.08) * mm, v(17.46, -61.4) * mm, v(17.98, -61.41) * mm, v(18.6, -60.92) * mm, v(18.98, -60.49) * mm, v(18.98, -60.3) * mm, v(18.98, -59.79) * mm, v(18.98, -59.47) * mm]});
            skFitSpline(sketch, "E77", {"points": [v(19.4, -59.18) * mm, v(19.23, -59.38) * mm, v(19.19, -59.7) * mm, v(19.23, -59.98) * mm, v(19.44, -59.7) * mm, v(19.4, -59.18) * mm]});
            skFitSpline(sketch, "E78", {"points": [v(6.03, -50.9) * mm, v(5.56, -51.02) * mm, v(4.9, -51.3) * mm, v(4.35, -51.76) * mm, v(4.11, -52.5) * mm, v(4.36, -53.11) * mm, v(4.78, -53.54) * mm, v(5.45, -53.8) * mm, v(6.06, -53.83) * mm], "startDerivative": vector(-4.18, -0.84) * mm, "endDerivative": vector(4.97, 0.09) * mm});
            skFitSpline(sketch, "E79", {"points": [v(6.03, -50.9) * mm, v(6.03, -51.04) * mm, v(5.65, -51.13) * mm, v(5.2, -51.36) * mm, v(4.8, -51.7) * mm, v(4.53, -52.31) * mm, v(4.58, -52.88) * mm, v(4.93, -53.38) * mm, v(5.54, -53.63) * mm, v(6.2, -53.65) * mm], "startDerivative": vector(0.77, -2.73) * mm, "endDerivative": vector(5.22, 0.23) * mm});
            skFitSpline(sketch, "E80", {"points": [v(6.2, -53.65) * mm, v(6.38, -53.2) * mm, v(6.66, -52.43) * mm, v(7.12, -51.32) * mm, v(7.8, -50.33) * mm, v(8.5, -49.87) * mm, v(9.14, -49.87) * mm, v(9.5, -50.18) * mm, v(9.53, -50.9) * mm, v(9.23, -51.74) * mm, v(8.64, -52.57) * mm, v(7.9, -53.22) * mm, v(7.12, -53.65) * mm, v(6.4, -53.8) * mm], "startDerivative": vector(3.1, 7.1) * mm, "endDerivative": vector(-9.94, -1.35) * mm});
            skFitSpline(sketch, "E81", {"points": [v(6.54, -53.53) * mm, v(7.01, -52.55) * mm, v(7.39, -51.85) * mm, v(7.97, -50.98) * mm, v(8.5, -50.45) * mm, v(8.84, -50.22) * mm, v(9.18, -50.28) * mm, v(9.22, -50.67) * mm, v(9.04, -51.47) * mm, v(8.67, -52.05) * mm, v(8.12, -52.7) * mm, v(7.58, -53.13) * mm, v(6.87, -53.48) * mm, v(6.54, -53.53) * mm]});
            skFitSpline(sketch, "E82", {"points": [v(10.93, -53.14) * mm, v(10.56, -52.95) * mm, v(10.13, -52.82) * mm, v(9.6, -52.82) * mm, v(9.05, -53.06) * mm, v(8.6, -53.8) * mm, v(8.53, -54.58) * mm, v(8.87, -55.24) * mm], "startDerivative": vector(-3.06, 1.72) * mm, "endDerivative": vector(2.72, -4.1) * mm});
            skFitSpline(sketch, "E83", {"points": [v(8.87, -55.24) * mm, v(9.27, -55.62) * mm, v(9.64, -55.72) * mm, v(10.07, -55.69) * mm, v(10.57, -55.4) * mm, v(10.96, -54.85) * mm, v(11.14, -55.24) * mm, v(11.4, -55.64) * mm, v(11.8, -55.78) * mm, v(11.99, -55.65) * mm, v(11.96, -55.43) * mm, v(11.67, -55.37) * mm, v(11.33, -54.74) * mm, v(11.22, -54.48) * mm, v(11.4, -54.23) * mm, v(11.54, -53.82) * mm, v(11.6, -53.3) * mm, v(11.5, -52.97) * mm, v(11.25, -52.88) * mm, v(10.93, -53.14) * mm], "startDerivative": vector(6.3, -7.4) * mm, "endDerivative": vector(-6.03, -6.71) * mm});
            skFitSpline(sketch, "E84", {"points": [v(10.82, -53.5) * mm, v(10.56, -53.32) * mm, v(10.12, -53.14) * mm, v(9.63, -53.14) * mm, v(9.17, -53.42) * mm, v(8.87, -54.07) * mm, v(8.87, -54.58) * mm, v(9.22, -55.24) * mm, v(9.75, -55.4) * mm, v(10.44, -55.03) * mm, v(10.93, -54.5) * mm], "startDerivative": vector(-3.19, 2.47) * mm, "endDerivative": vector(3.85, 5) * mm});
            skFitSpline(sketch, "E85", {"points": [v(6.06, -53.83) * mm, v(5.81, -54.32) * mm, v(5.5, -54.81) * mm, v(5.27, -55.18) * mm, v(5.2, -55.26) * mm, v(4.84, -55.23) * mm, v(4.25, -55.23) * mm, v(3.36, -55.37) * mm, v(2.57, -55.77) * mm, v(2.26, -56.3) * mm, v(2.42, -56.72) * mm, v(2.8, -57.03) * mm, v(3.71, -57.08) * mm, v(4.7, -56.45) * mm, v(5.33, -55.7) * mm], "startDerivative": vector(-3.5, -7.21) * mm, "endDerivative": vector(6.36, 8.24) * mm});
            skFitSpline(sketch, "E86", {"points": [v(5.02, -55.61) * mm, v(4.56, -56.18) * mm, v(4.13, -56.6) * mm, v(3.47, -56.86) * mm, v(2.65, -56.74) * mm, v(2.46, -56.37) * mm, v(2.9, -55.9) * mm, v(3.68, -55.63) * mm, v(4.58, -55.55) * mm, v(5.02, -55.61) * mm]});
            skFitSpline(sketch, "E87", {"points": [v(5.63, -55.3) * mm, v(6.18, -54.33) * mm, v(6.4, -53.8) * mm], "startDerivative": vector(1.09, 1.78) * mm, "endDerivative": vector(0.4, 1.2) * mm});
            skFitSpline(sketch, "E88", {"points": [v(5.33, -55.7) * mm, v(5.87, -55.82) * mm, v(6.76, -56.04) * mm, v(7.7, -56.48) * mm, v(8.34, -57.14) * mm, v(8.48, -57.82) * mm, v(8.33, -58.38) * mm, v(8.43, -58.45) * mm, v(8.78, -58.12) * mm, v(8.78, -57.48) * mm, v(8.46, -56.82) * mm, v(7.66, -56.19) * mm, v(6.32, -55.51) * mm, v(5.63, -55.3) * mm], "startDerivative": vector(7.5, -1.6) * mm, "endDerivative": vector(-8.21, 1.98) * mm});
            skFitSpline(sketch, "E89", {"points": [v(10.82, -53.5) * mm, v(10.82, -54.03) * mm, v(10.82, -54.5) * mm, v(10.78, -54.68) * mm], "startDerivative": vector(-0.01, -1.33) * mm, "endDerivative": vector(-0.18, -0.7) * mm});
            skLineSegment(sketch, "E90.bottom", {"start": v(-33.81, -40.5) * mm, "end": v(34.77, -40.5) * mm});
            skLineSegment(sketch, "E90.top", {"start": v(-33.81, -84.94) * mm, "end": v(34.77, -84.94) * mm});
            skLineSegment(sketch, "E90.left", {"start": v(-33.81, -40.5) * mm, "end": v(-33.81, -84.94) * mm});
            skLineSegment(sketch, "E90.right", {"start": v(34.77, -40.5) * mm, "end": v(34.77, -84.94) * mm});
            skLineSegment(sketch, "E91", {"start": v(15.29, -53.34) * mm, "end": v(15.27, -53.25) * mm});
            skLineSegment(sketch, "E92", {"start": v(13.83, -64.36) * mm, "end": v(14.67, -64.93) * mm});
            skSolve(sketch);
        }
        {
            var Q0;
            Q0=makeQuery(id+"F2.imprint","IMPRINT",FACE,{"disambiguationData":[TD([[makeQuery(id+"F2.imprint","IMPRINT",EDGE,{"derivedFrom":sQuery(id+"F2.wireOp",EDGE,"E59")}),-1.0]])]});
            var Q1;
            Q1=makeQuery(id+"F2.imprint","IMPRINT",FACE,{"disambiguationData":[TD([[makeQuery(id+"F2.imprint","IMPRINT",EDGE,{"derivedFrom":sQuery(id+"F2.wireOp",EDGE,"E66")}),-1.0]])]});
            var Q2;
            Q2=makeQuery(id+"F2.imprint","IMPRINT",FACE,{"disambiguationData":[TD([[makeQuery(id+"F2.imprint","IMPRINT",EDGE,{"derivedFrom":sQuery(id+"F2.wireOp",EDGE,"E69")}),1.0]])]});
            var Q3;
            Q3=makeQuery(id+"F2.imprint","IMPRINT",FACE,{"disambiguationData":[TD([[makeQuery(id+"F2.imprint","IMPRINT",EDGE,{"derivedFrom":sQuery(id+"F2.wireOp",EDGE,"E70")}),-1.0]])]});
            var Q4;
            Q4=makeQuery(id+"F2.imprint","IMPRINT",FACE,{"disambiguationData":[TD([[makeQuery(id+"F2.imprint","IMPRINT",EDGE,{"derivedFrom":sQuery(id+"F2.wireOp",EDGE,"E71")}),1.0]])]});
            var Q5;
            Q5=makeQuery(id+"F2.imprint","IMPRINT",FACE,{"disambiguationData":[TD([[makeQuery(id+"F2.imprint","IMPRINT",EDGE,{"derivedFrom":sQuery(id+"F2.wireOp",EDGE,"E73")}),-1.0]])]});
            var Q6;
            Q6=makeQuery(id+"F2.imprint","IMPRINT",FACE,{"disambiguationData":[TD([[makeQuery(id+"F2.imprint","IMPRINT",EDGE,{"derivedFrom":sQuery(id+"F2.wireOp",EDGE,"E5")}),-1.0]])]});
            var Q7;
            Q7=makeQuery(id+"F2.imprint","IMPRINT",FACE,{"disambiguationData":[TD([[makeQuery(id+"F2.imprint","IMPRINT",EDGE,{"derivedFrom":sQuery(id+"F2.wireOp",EDGE,"E75")}),1.0]])]});
            var Q8;
            Q8=makeQuery(id+"F2.imprint","IMPRINT",FACE,{"disambiguationData":[TD([[makeQuery(id+"F2.imprint","IMPRINT",EDGE,{"derivedFrom":sQuery(id+"F2.wireOp",EDGE,"E78")}),1.0]])]});
            var Q9;
            Q9=makeQuery(id+"F2.imprint","IMPRINT",FACE,{"disambiguationData":[TD([[makeQuery(id+"F2.imprint","IMPRINT",EDGE,{"derivedFrom":sQuery(id+"F2.wireOp",EDGE,"E82")}),1.0]])]});
            var Q10;
            Q10=makeQuery(id+"F2.imprint","IMPRINT",FACE,{"disambiguationData":[TD([[makeQuery(id+"F2.imprint","IMPRINT",EDGE,{"derivedFrom":sQuery(id+"F2.wireOp",EDGE,"E54")}),-1.0]])]});
            extrude(context, id + "F3", {"entities" : qUnion([Q0, Q1, Q2, Q3, Q4, Q5, Q6, Q7, Q8, Q9, Q10]), "operationType" : NewBodyOperationType.REMOVE, "endBound" : BoundingType.THROUGH_ALL, "depth" : 25.4 * mm, "offsetDistance" : 25.4 * mm});
        }
        {
            var Q0;
            {var subQ3=sQuery(id+"F0.wireOp",EDGE,"E0.top");var subQ4=sQuery(id+"F0.wireOp",EDGE,"E0.right");var subQ6=sQuery(id+"F0.wireOp",EDGE,"E0.bottom");var subQ7=sQuery(id+"F0.wireOp",EDGE,"E1");var subQ8=sQuery(id+"F0.wireOp",EDGE,"E0.left");Q0=makeQuery(id+"F3.boolean.opBoolean","SPLIT",FACE,{"disambiguationData":[TD([makeQuery(id+"F1.opExtrude","SWEPT_FACE",FACE,{"disambiguationData":[OSD([subQ6])]})])],"derivedFrom":makeQuery(id+"F1.opExtrude","CAP_FACE",FACE,{"disambiguationData":[OSD([subQ6,subQ3,subQ8,subQ4,subQ7])],"isStart":false})});}
            var sketch = newSketch(context, id + "F4", { "sketchPlane" : qUnion([Q0])});
            skArc(sketch, "E93", {"start": v(16.82, -52.3) * mm, "mid": v(16.51, -51.34) * mm, "end": v(15.65, -50.84) * mm});
            skArc(sketch, "E94", {"start": v(14.05, -51.6) * mm, "mid": v(14.25, -52.73) * mm, "end": v(15.27, -53.25) * mm});
            skFitSpline(sketch, "E95.0", {"points": [v(13.96, -51.96) * mm, v(13.94, -52.12) * mm, v(13.97, -52.55) * mm, v(14.46, -52.97) * mm, v(14.94, -53.28) * mm, v(15.66, -53.26) * mm, v(16.39, -52.95) * mm, v(16.77, -52.6) * mm, v(16.9, -51.92) * mm, v(16.74, -51.43) * mm, v(16.3, -51.02) * mm, v(15.66, -50.78) * mm, v(14.8, -50.84) * mm, v(14.33, -51.15) * mm, v(14.03, -51.6) * mm, v(13.97, -51.83) * mm, v(13.96, -51.96) * mm]});
            skFitSpline(sketch, "E96.0", {"points": [v(13.96, -51.96) * mm, v(13.94, -52.12) * mm, v(13.97, -52.55) * mm, v(14.46, -52.97) * mm, v(14.94, -53.28) * mm, v(15.66, -53.26) * mm, v(16.39, -52.95) * mm, v(16.77, -52.6) * mm, v(16.9, -51.92) * mm, v(16.74, -51.43) * mm, v(16.3, -51.02) * mm, v(15.66, -50.78) * mm, v(14.8, -50.84) * mm, v(14.33, -51.15) * mm, v(14.03, -51.6) * mm, v(13.97, -51.83) * mm, v(13.96, -51.96) * mm]});
            skSolve(sketch);
        }
        {
            var Q0;
            Q0=makeQuery(id+"F4.imprint","IMPRINT",FACE,{"disambiguationData":[TD([[makeQuery(id+"F4.imprint","IMPRINT",EDGE,{"derivedFrom":sQuery(id+"F4.wireOp",EDGE,"E93")}),1.0]])]});
            extrude(context, id + "F5", {"entities" : qUnion([Q0]), "operationType" : NewBodyOperationType.REMOVE, "oppositeDirection" : true, "depth" : 0.25 * mm, "offsetDistance" : 25.4 * mm});
        }
    });
